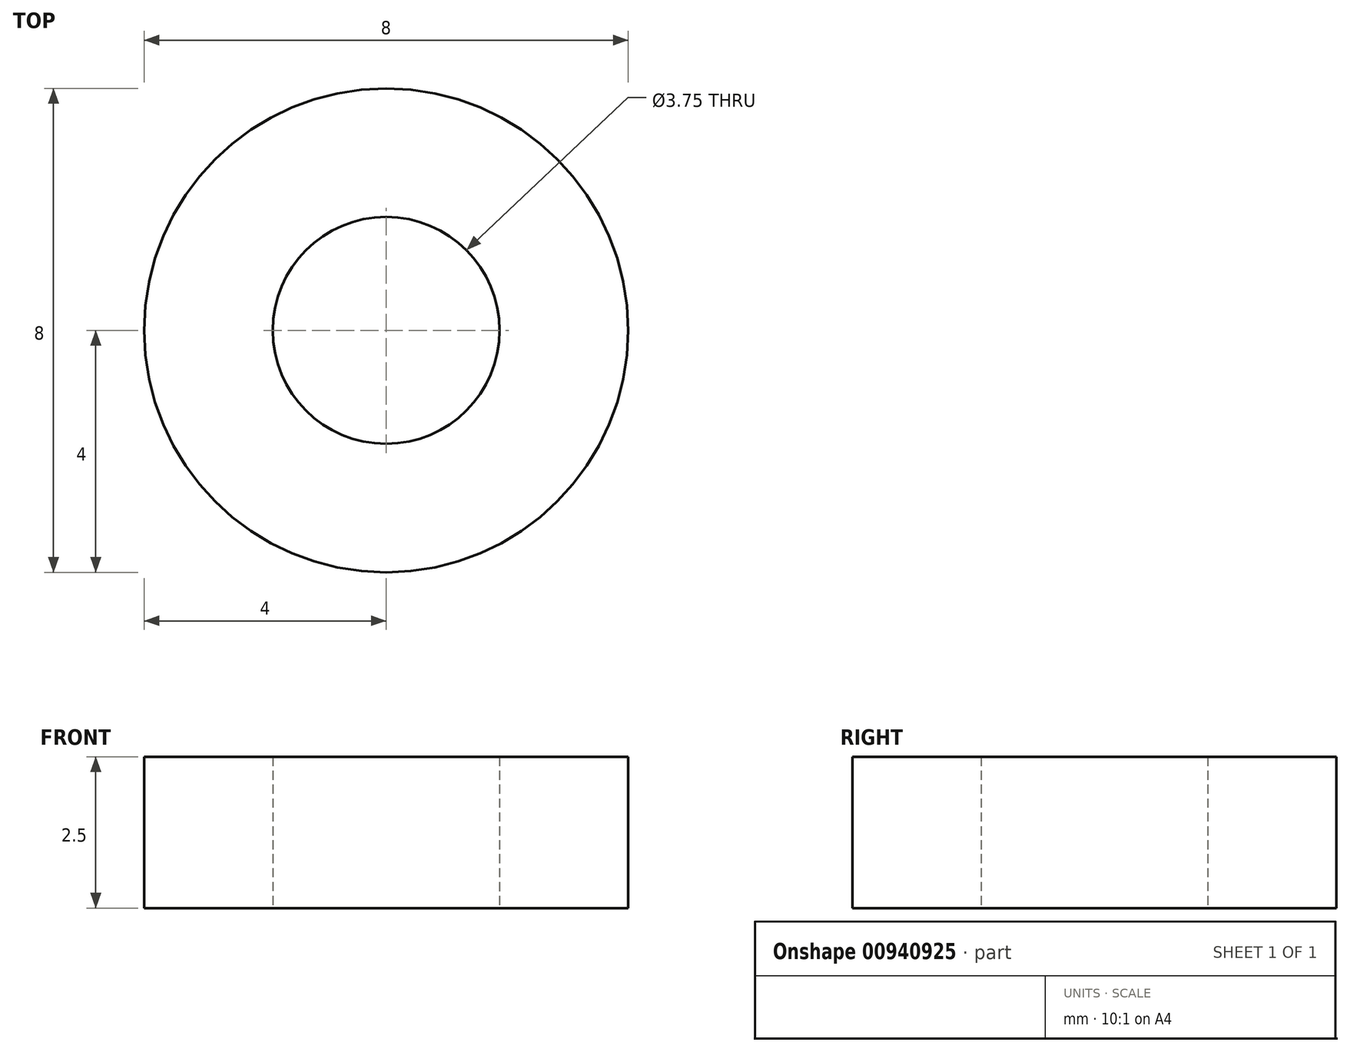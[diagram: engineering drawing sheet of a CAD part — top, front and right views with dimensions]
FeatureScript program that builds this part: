
annotation { "Feature Type Name" : "Feature", "Feature Type Description" : "" }
export const myFeature = defineFeature(function(context is Context, id is Id, definition is map)
    precondition{}
    {
        {
            var Q0;
            Q0=qCreatedBy(makeId("Top.planeOp"),FACE);
            var sketch = newSketch(context, id + "F0", { "sketchPlane" : qUnion([Q0])});
            skCircle(sketch, "E0", {"center": v(0, 0) * mm, "radius": 4 * mm});
            skCircle(sketch, "E1", {"center": v(0, 0) * mm, "radius": 1.88 * mm});
            skSolve(sketch);
        }
        {
            var Q0;
            Q0=makeQuery(id+"F0.imprint","IMPRINT",FACE,{"disambiguationData":[TD([[makeQuery(id+"F0.imprint","IMPRINT",EDGE,{"derivedFrom":sQuery(id+"F0.wireOp",EDGE,"E0")}),1.0]])]});
            extrude(context, id + "F1", {"entities" : qUnion([Q0]), "depth" : 2.5 * mm, "offsetDistance" : 25 * mm});
        }
    });
